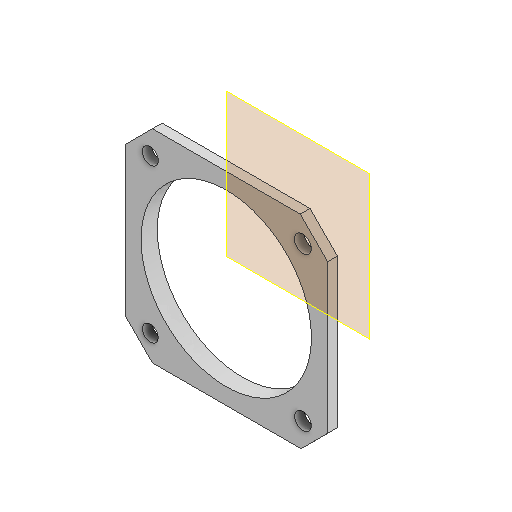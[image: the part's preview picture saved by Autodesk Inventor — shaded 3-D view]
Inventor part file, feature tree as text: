
AUTODESK INVENTOR PART (.ipt)
format: ipt  version: 2022 (Build 260153000, 153)  size: 148,480 bytes
history: native  units: mm
features: extrude x2, sketch x2, plane x1
ambient origin geometry x8: Origin, YZ Plane, XZ Plane, XY Plane, X Axis, Y Axis, Z Axis, Center Point
bodies: Volumenkörper1 (feature_tree)
feature tree (5):
  plane  "Arbeitsebene1"
  extrude  "Extrusion1"  Depth=1.5mm
  extrude  "Extrusion2"  [1 undecoded]
  sketch  "Skizze1"  dims[d0=1.5mm d1=0.0mm d2=28.0mm]
  sketch  "Skizze2"  dims[d3=1.0mm d4=0.0mm]
note: 1 required parameter value undecoded (feature->parameter linkage not recoverable at this tier; creation-order binding heuristic only, values carry confidence <= 0.55)
